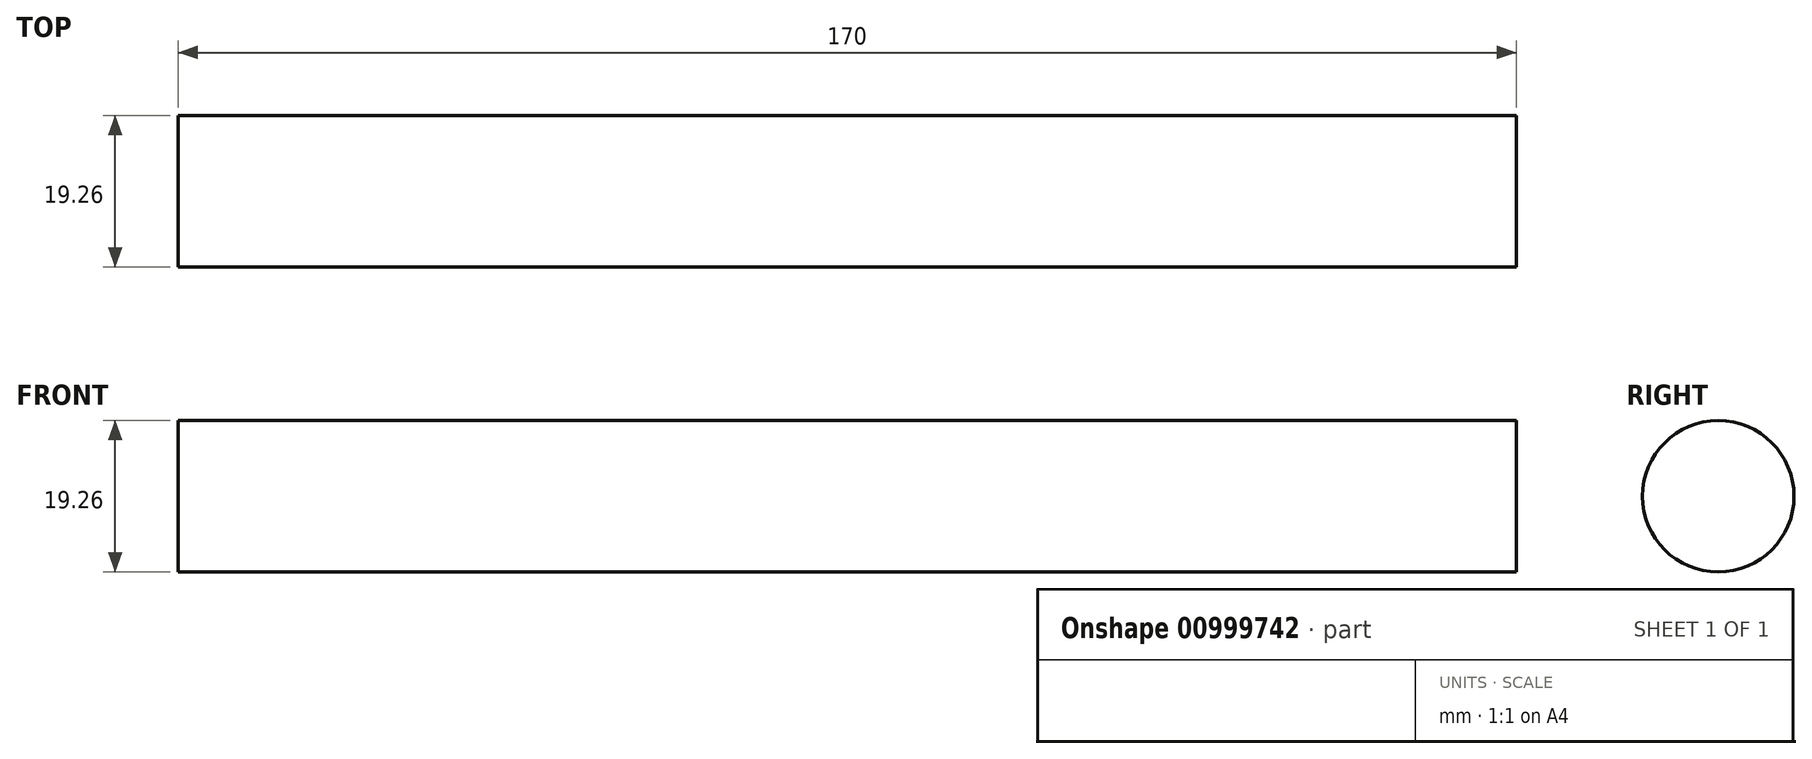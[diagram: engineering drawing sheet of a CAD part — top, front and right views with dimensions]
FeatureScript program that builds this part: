
annotation { "Feature Type Name" : "Feature", "Feature Type Description" : "" }
export const myFeature = defineFeature(function(context is Context, id is Id, definition is map)
    precondition{}
    {
        {
            var Q0;
            Q0=qCreatedBy(makeId("Right.planeOp"),FACE);
            var sketch = newSketch(context, id + "F0", { "sketchPlane" : qUnion([Q0])});
            skCircle(sketch, "E0", {"center": v(0, 0) * mm, "radius": 9.62 * mm});
            skSolve(sketch);
        }
        {
            var Q0;
            Q0=makeQuery(id+"F0.imprint","IMPRINT",FACE,{"disambiguationData":[TD([[makeQuery(id+"F0.imprint","IMPRINT",EDGE,{"derivedFrom":sQuery(id+"F0.wireOp",EDGE,"E0")}),1.0]])]});
            extrude(context, id + "F1", {"entities" : qUnion([Q0]), "endBound" : BoundingType.SYMMETRIC, "depth" : 170 * mm, "offsetDistance" : 25 * mm});
        }
    });
